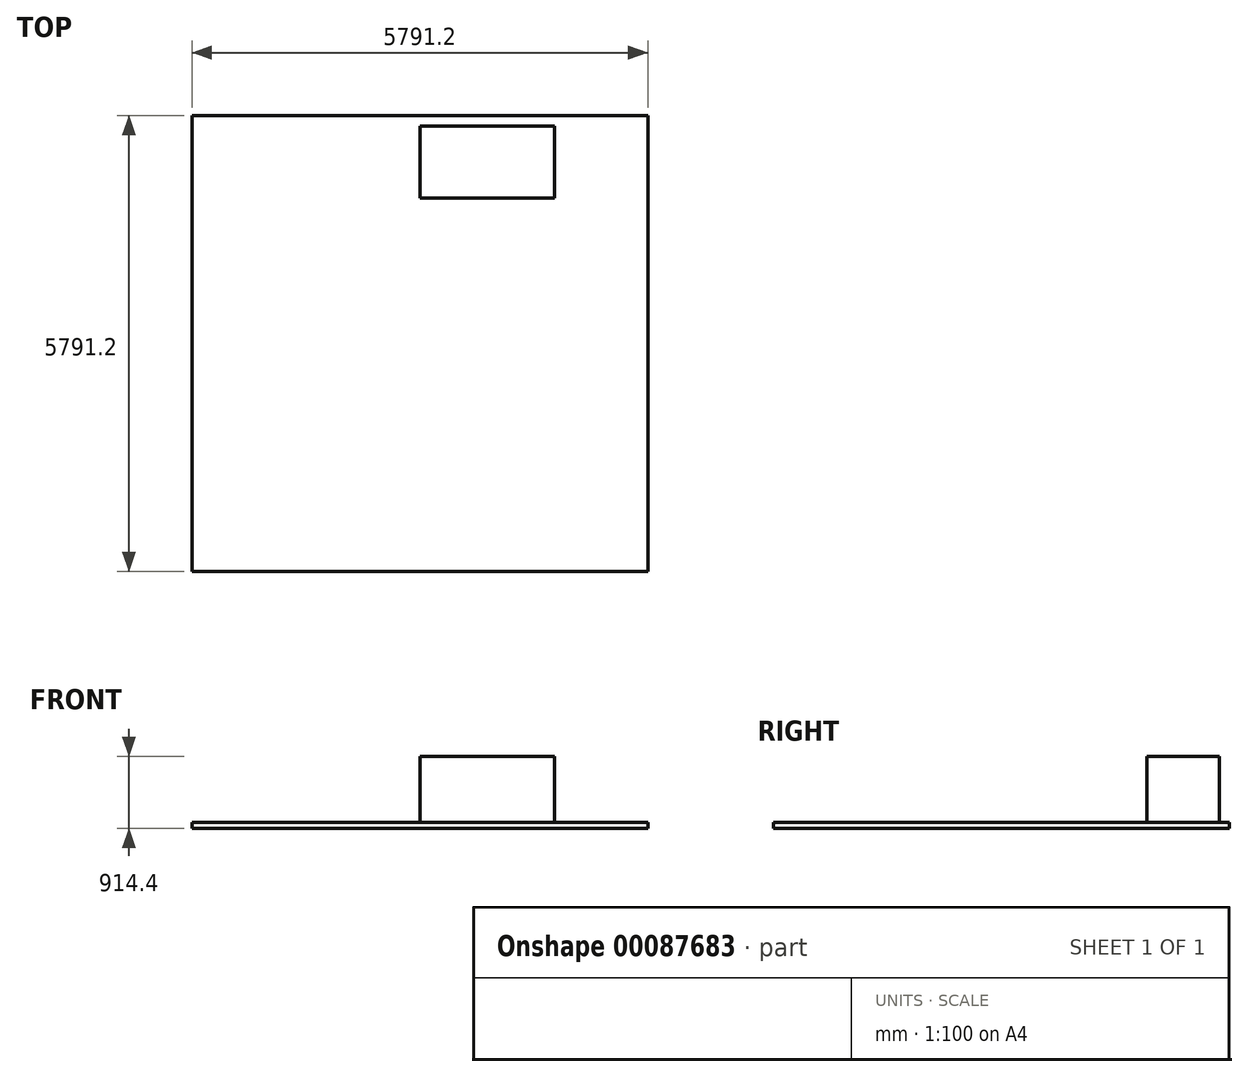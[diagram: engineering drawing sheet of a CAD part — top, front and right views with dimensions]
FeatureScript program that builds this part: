
annotation { "Feature Type Name" : "Feature", "Feature Type Description" : "" }
export const myFeature = defineFeature(function(context is Context, id is Id, definition is map)
    precondition{}
    {
        {
            var Q0;
            Q0=qCreatedBy(makeId("Top.planeOp"),FACE);
            var sketch = newSketch(context, id + "F0", { "sketchPlane" : qUnion([Q0])});
            skLineSegment(sketch, "E0.bottom", {"start": v(-2897.27, 3439.39) * mm, "end": v(2893.93, 3439.39) * mm});
            skLineSegment(sketch, "E0.top", {"start": v(-2897.27, -2351.81) * mm, "end": v(2893.93, -2351.81) * mm});
            skLineSegment(sketch, "E0.left", {"start": v(-2897.27, 3439.39) * mm, "end": v(-2897.27, -2351.81) * mm});
            skLineSegment(sketch, "E0.right", {"start": v(2893.93, 3439.39) * mm, "end": v(2893.93, -2351.81) * mm});
            skSolve(sketch);
        }
        {
            var Q0;
            Q0 = qSketchRegion(id + "F0", true);
            extrude(context, id + "F1", {"entities" : qUnion([Q0]), "depth" : 2438.4 * mm});
        }
        {
            var Q0;
            Q0=makeQuery(id+"F1.opExtrude","CAP_FACE",FACE,{"disambiguationData":[OSD([sQuery(id+"F0.wireOp",EDGE,"E0.bottom"),sQuery(id+"F0.wireOp",EDGE,"E0.top"),sQuery(id+"F0.wireOp",EDGE,"E0.left"),sQuery(id+"F0.wireOp",EDGE,"E0.right")])],"isStart":false});
            var Q1;
            Q1=makeQuery(id+"F1.opExtrude","SWEPT_FACE",FACE,{"disambiguationData":[OSD([sQuery(id+"F0.wireOp",EDGE,"E0.right")])]});
            var Q2;
            Q2=makeQuery(id+"F1.opExtrude","SWEPT_FACE",FACE,{"disambiguationData":[OSD([sQuery(id+"F0.wireOp",EDGE,"E0.top")])]});
            var Q3;
            Q3=makeQuery(id+"F1.opExtrude","SWEPT_FACE",FACE,{"disambiguationData":[OSD([sQuery(id+"F0.wireOp",EDGE,"E0.bottom")])]});
            var Q4;
            Q4=makeQuery(id+"F1.opExtrude","SWEPT_FACE",FACE,{"disambiguationData":[OSD([sQuery(id+"F0.wireOp",EDGE,"E0.left")])]});
            var Q5;
            Q5=makeQuery(id+"F1.opExtrude","SWEPT_BODY",BODY,{"disambiguationData":[OSD([sQuery(id+"F0.wireOp",EDGE,"E0.bottom"),sQuery(id+"F0.wireOp",EDGE,"E0.top"),sQuery(id+"F0.wireOp",EDGE,"E0.left"),sQuery(id+"F0.wireOp",EDGE,"E0.right")])]});
            shell(context, id + "F2", {"entities" : qUnion([Q0, Q1, Q2, Q3, Q4]), "parts" : qUnion([Q5]), "thickness" : 76.2 * mm});
        }
        {
            var Q0;
            Q0=qCreatedBy(makeId("Top.planeOp"),FACE);
            var sketch = newSketch(context, id + "F3", { "sketchPlane" : qUnion([Q0])});
            skLineSegment(sketch, "E1.bottom", {"start": v(0, 3306.6) * mm, "end": v(853.44, 3306.6) * mm});
            skLineSegment(sketch, "E1.top", {"start": v(0, 2392.2) * mm, "end": v(853.44, 2392.2) * mm});
            skLineSegment(sketch, "E1.left", {"start": v(0, 3306.6) * mm, "end": v(0, 2392.2) * mm});
            skLineSegment(sketch, "E1.right", {"start": v(853.44, 3306.6) * mm, "end": v(853.44, 2392.2) * mm});
            skLineSegment(sketch, "E2.bottom", {"start": v(853.44, 3306.6) * mm, "end": v(1706.88, 3306.6) * mm});
            skLineSegment(sketch, "E2.top", {"start": v(853.44, 2392.2) * mm, "end": v(1706.88, 2392.2) * mm});
            skLineSegment(sketch, "E2.right", {"start": v(1706.88, 3306.6) * mm, "end": v(1706.88, 2392.2) * mm});
            skSolve(sketch);
        }
        {
            var Q0;
            Q0 = qSketchRegion(id + "F3", true);
            extrude(context, id + "F4", {"entities" : qUnion([Q0]), "operationType" : NewBodyOperationType.ADD, "depth" : 914.4 * mm});
        }
    });
